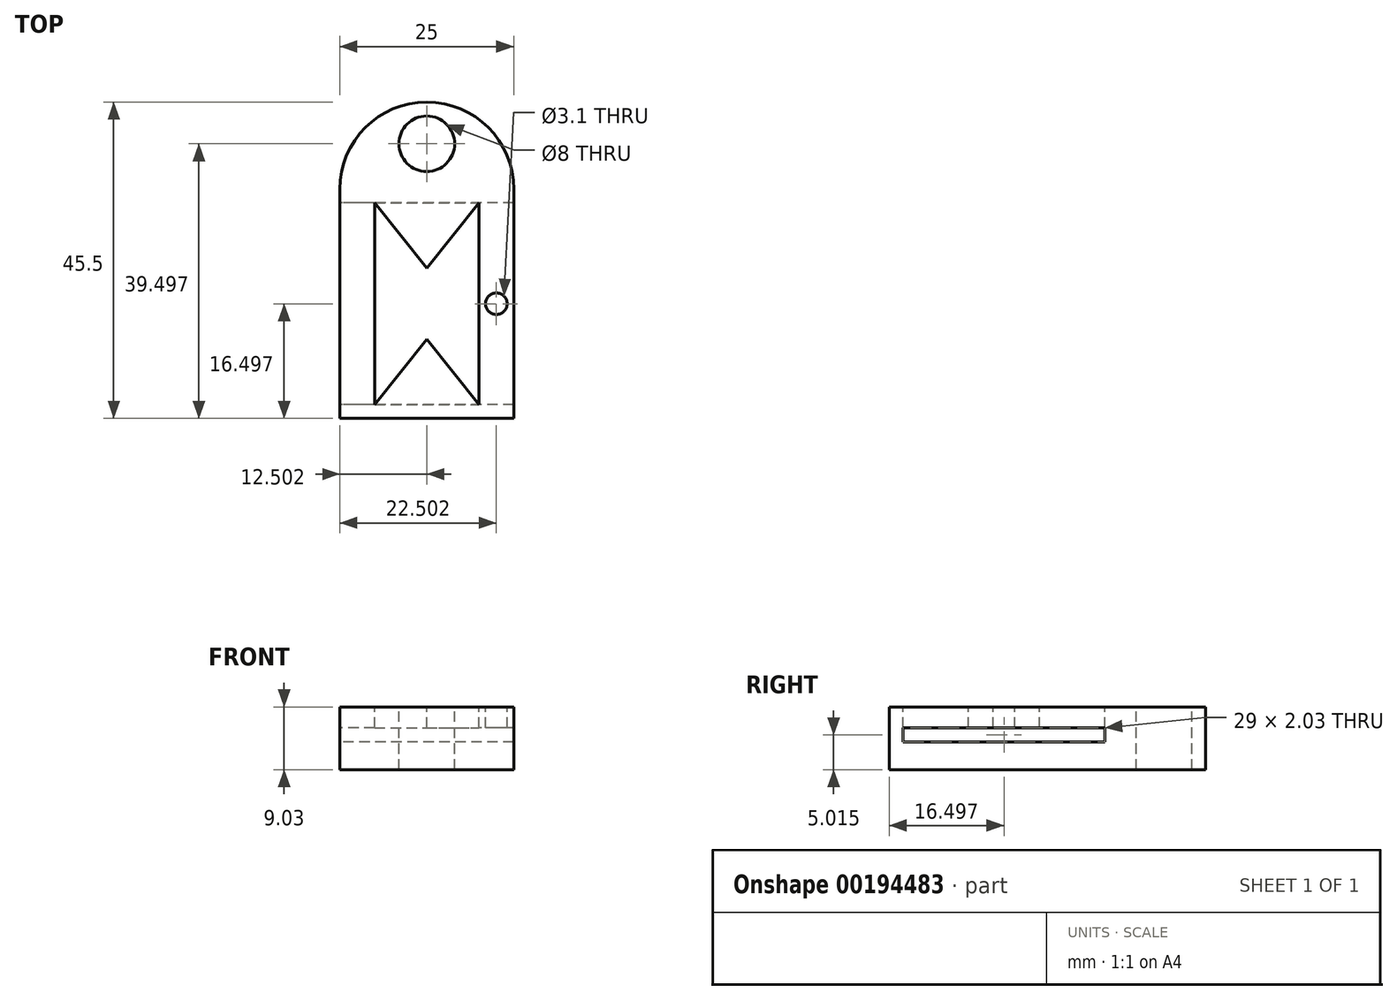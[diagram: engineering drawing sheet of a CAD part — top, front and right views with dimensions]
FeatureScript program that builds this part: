
annotation { "Feature Type Name" : "Feature", "Feature Type Description" : "" }
export const myFeature = defineFeature(function(context is Context, id is Id, definition is map)
    precondition{}
    {
        {
            var Q0;
            Q0=qCreatedBy(makeId("Top.planeOp"),FACE);
            var sketch = newSketch(context, id + "F0", { "sketchPlane" : qUnion([Q0])});
            skLineSegment(sketch, "E0.bottom", {"start": v(-9.59, 18.7) * mm, "end": v(15.41, 18.7) * mm});
            skLineSegment(sketch, "E0.top", {"start": v(-9.59, -14.3) * mm, "end": v(15.41, -14.3) * mm});
            skLineSegment(sketch, "E0.left", {"start": v(-9.59, 18.7) * mm, "end": v(-9.59, -14.3) * mm});
            skLineSegment(sketch, "E0.right", {"start": v(15.41, 18.7) * mm, "end": v(15.41, -14.3) * mm});
            skCircle(sketch, "E1", {"center": v(2.91, 18.7) * mm, "radius": 12.5 * mm});
            skSolve(sketch);
        }
        {
            var Q0;
            {var subQ0=sQuery(id+"F0.wireOp",EDGE,"E0.bottom");Q0=makeQuery(id+"F0.imprint","IMPRINT",FACE,{"disambiguationData":[TD([[makeQuery(id+"F0.imprint","IMPRINT",EDGE,{"derivedFrom":subQ0}),1.0]])]});}
            var Q1;
            {var subQ0=sQuery(id+"F0.wireOp",EDGE,"E0.bottom");Q1=makeQuery(id+"F0.imprint","IMPRINT",FACE,{"disambiguationData":[TD([[makeQuery(id+"F0.imprint","IMPRINT",EDGE,{"derivedFrom":subQ0}),-1.0]])]});}
            var Q2;
            Q2=makeQuery(id+"F0.imprint","IMPRINT",FACE,{"disambiguationData":[TD([[makeQuery(id+"F0.imprint","IMPRINT",EDGE,{"derivedFrom":sQuery(id+"F0.wireOp",EDGE,"E0.top")}),1.0]])]});
            extrude(context, id + "F1", {"entities" : qUnion([Q0, Q1, Q2]), "depth" : 9.03 * mm});
        }
        {
            var Q0;
            Q0=makeQuery(id+"F1.opExtrude","SWEPT_FACE",FACE,{"disambiguationData":[OSD([sQuery(id+"F0.wireOp",EDGE,"E0.left")])]});
            var sketch = newSketch(context, id + "F2", { "sketchPlane" : qUnion([Q0])});
            skLineSegment(sketch, "E2.bottom", {"start": v(12.3, 4) * mm, "end": v(-16.7, 4) * mm});
            skLineSegment(sketch, "E2.top", {"start": v(12.3, 6.03) * mm, "end": v(-16.7, 6.03) * mm});
            skLineSegment(sketch, "E2.left", {"start": v(12.3, 4) * mm, "end": v(12.3, 6.03) * mm});
            skLineSegment(sketch, "E2.right", {"start": v(-16.7, 4) * mm, "end": v(-16.7, 6.03) * mm});
            skSolve(sketch);
        }
        {
            var Q0;
            Q0 = qSketchRegion(id + "F2", true);
            extrude(context, id + "F3", {"entities" : qUnion([Q0]), "operationType" : NewBodyOperationType.REMOVE, "endBound" : BoundingType.THROUGH_ALL, "oppositeDirection" : true, "depth" : 25 * mm});
        }
        {
            var Q0;
            Q0=makeQuery(id+"F1.opExtrude","CAP_FACE",FACE,{"disambiguationData":[OSD([sQuery(id+"F0.wireOp",EDGE,"E0.top"),sQuery(id+"F0.wireOp",EDGE,"E0.left"),sQuery(id+"F0.wireOp",EDGE,"E0.right"),sQuery(id+"F0.wireOp",EDGE,"E1")])],"isStart":false});
            var sketch = newSketch(context, id + "F4", { "sketchPlane" : qUnion([Q0])});
            skLineSegment(sketch, "E3.bottom", {"start": v(-4.59, -12.3) * mm, "end": v(10.41, -12.3) * mm});
            skLineSegment(sketch, "E3.top", {"start": v(-4.59, 16.7) * mm, "end": v(10.41, 16.7) * mm});
            skLineSegment(sketch, "E3.left", {"start": v(-4.59, -12.3) * mm, "end": v(-4.59, 16.7) * mm});
            skLineSegment(sketch, "E3.right", {"start": v(10.41, -12.3) * mm, "end": v(10.41, 16.7) * mm});
            skSolve(sketch);
        }
        {
            var Q0;
            Q0 = qSketchRegion(id + "F4", true);
            extrude(context, id + "F5", {"entities" : qUnion([Q0]), "operationType" : NewBodyOperationType.REMOVE, "endBound" : BoundingType.UP_TO_NEXT, "oppositeDirection" : true, "depth" : 25 * mm});
        }
        {
            var Q0;
            Q0=makeQuery(id+"F1.opExtrude","CAP_FACE",FACE,{"disambiguationData":[OSD([sQuery(id+"F0.wireOp",EDGE,"E0.top"),sQuery(id+"F0.wireOp",EDGE,"E0.left"),sQuery(id+"F0.wireOp",EDGE,"E0.right"),sQuery(id+"F0.wireOp",EDGE,"E1")])],"isStart":false});
            var sketch = newSketch(context, id + "F6", { "sketchPlane" : qUnion([Q0])});
            skLineSegment(sketch, "E4", {"start": v(-4.59, 16.7) * mm, "end": v(2.91, 7.33) * mm});
            skLineSegment(sketch, "E5", {"start": v(2.91, 7.33) * mm, "end": v(10.41, 16.7) * mm});
            skLineSegment(sketch, "E6", {"start": v(-4.59, -12.3) * mm, "end": v(2.91, -2.94) * mm});
            skLineSegment(sketch, "E7", {"start": v(2.91, -2.94) * mm, "end": v(10.41, -12.3) * mm});
            skSolve(sketch);
        }
        {
            var Q0;
            Q0 = qSketchRegion(id + "F6", true);
            var Q1;
            Q1=makeQuery(id+"F6.imprint","IMPRINT",FACE,{"disambiguationData":[TD([[makeQuery(id+"F6.imprint","IMPRINT",EDGE,{"derivedFrom":sQuery(id+"F6.wireOp",EDGE,"E6")}),-1.0]])]});
            var Q2;
            Q2=makeQuery(id+"F6.imprint","IMPRINT",FACE,{"disambiguationData":[TD([[makeQuery(id+"F6.imprint","IMPRINT",EDGE,{"derivedFrom":sQuery(id+"F6.wireOp",EDGE,"E4")}),1.0]])]});
            extrude(context, id + "F7", {"entities" : qUnion([Q0, Q1, Q2]), "operationType" : NewBodyOperationType.ADD, "oppositeDirection" : true, "depth" : 3 * mm});
        }
        {
            var Q0;
            Q0=makeQuery(id+"F7.boolean.opBoolean","MERGE",FACE,{"derivedFrom":[makeQuery(id+"F1.opExtrude","CAP_FACE",FACE,{"disambiguationData":[OSD([sQuery(id+"F0.wireOp",EDGE,"E0.top"),sQuery(id+"F0.wireOp",EDGE,"E0.left"),sQuery(id+"F0.wireOp",EDGE,"E0.right"),sQuery(id+"F0.wireOp",EDGE,"E1")])],"isStart":false}),makeQuery(id+"F7.opExtrude","CAP_FACE",FACE,{"disambiguationData":[OSD([sQuery(id+"F4.wireOp",EDGE,"E3.top"),sQuery(id+"F6.wireOp",EDGE,"E4"),sQuery(id+"F6.wireOp",EDGE,"E5")])],"isStart":true}),makeQuery(id+"F7.opExtrude","CAP_FACE",FACE,{"disambiguationData":[OSD([sQuery(id+"F4.wireOp",EDGE,"E3.bottom"),sQuery(id+"F6.wireOp",EDGE,"E6"),sQuery(id+"F6.wireOp",EDGE,"E7")])],"isStart":true})]});
            var sketch = newSketch(context, id + "F8", { "sketchPlane" : qUnion([Q0])});
            skCircle(sketch, "E8", {"center": v(12.91, 2.2) * mm, "radius": 1.55 * mm});
            skSolve(sketch);
        }
        {
            var Q0;
            Q0 = qSketchRegion(id + "F8", true);
            extrude(context, id + "F9", {"entities" : qUnion([Q0]), "operationType" : NewBodyOperationType.REMOVE, "endBound" : BoundingType.UP_TO_NEXT, "oppositeDirection" : true, "depth" : 25 * mm});
        }
        {
            var Q0;
            Q0=makeQuery(id+"F7.boolean.opBoolean","MERGE",FACE,{"derivedFrom":[makeQuery(id+"F1.opExtrude","CAP_FACE",FACE,{"disambiguationData":[OSD([sQuery(id+"F0.wireOp",EDGE,"E0.top"),sQuery(id+"F0.wireOp",EDGE,"E0.left"),sQuery(id+"F0.wireOp",EDGE,"E0.right"),sQuery(id+"F0.wireOp",EDGE,"E1")])],"isStart":false}),makeQuery(id+"F7.opExtrude","CAP_FACE",FACE,{"disambiguationData":[OSD([sQuery(id+"F4.wireOp",EDGE,"E3.top"),sQuery(id+"F6.wireOp",EDGE,"E4"),sQuery(id+"F6.wireOp",EDGE,"E5")])],"isStart":true}),makeQuery(id+"F7.opExtrude","CAP_FACE",FACE,{"disambiguationData":[OSD([sQuery(id+"F4.wireOp",EDGE,"E3.bottom"),sQuery(id+"F6.wireOp",EDGE,"E6"),sQuery(id+"F6.wireOp",EDGE,"E7")])],"isStart":true})]});
            var sketch = newSketch(context, id + "F10", { "sketchPlane" : qUnion([Q0])});
            skCircle(sketch, "E9", {"center": v(2.91, 25.2) * mm, "radius": 4 * mm});
            skSolve(sketch);
        }
        {
            var Q0;
            Q0 = qSketchRegion(id + "F10", true);
            extrude(context, id + "F11", {"entities" : qUnion([Q0]), "operationType" : NewBodyOperationType.REMOVE, "endBound" : BoundingType.THROUGH_ALL, "oppositeDirection" : true, "depth" : 25 * mm});
        }
    });
